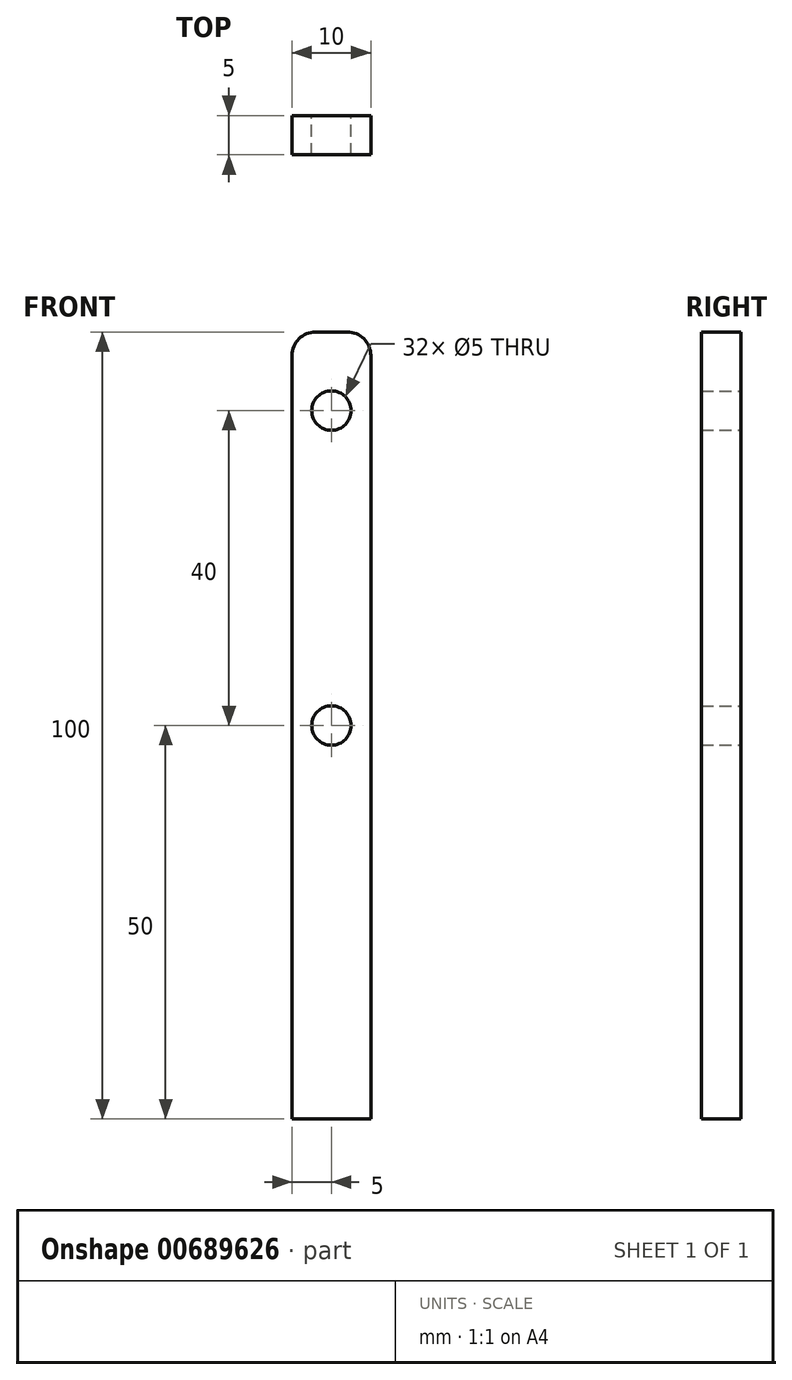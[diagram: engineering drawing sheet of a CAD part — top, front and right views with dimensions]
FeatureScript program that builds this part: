
annotation { "Feature Type Name" : "Feature", "Feature Type Description" : "" }
export const myFeature = defineFeature(function(context is Context, id is Id, definition is map)
    precondition{}
    {
        {
            var Q0;
            Q0=qCreatedBy(makeId("Front.planeOp"),FACE);
            var sketch = newSketch(context, id + "F0", { "sketchPlane" : qUnion([Q0])});
            skLineSegment(sketch, "E0", {"start": v(0, 0) * mm, "end": v(-10, 0) * mm});
            skLineSegment(sketch, "E1", {"start": v(-10, 0) * mm, "end": v(-10, 97) * mm});
            skLineSegment(sketch, "E2", {"start": v(-7, 100) * mm, "end": v(-3, 100) * mm});
            skLineSegment(sketch, "E3", {"start": v(0, 97) * mm, "end": v(0, 0) * mm});
            skCircle(sketch, "E4", {"center": v(-5, 50) * mm, "radius": 2.5 * mm});
            skCircle(sketch, "E5", {"center": v(-5, 90) * mm, "radius": 2.5 * mm});
            skPoint(sketch, "E6.visualSharp", {"position": v(0, 100) * mm});
            skArc(sketch, "E6.filletArc", {"start": v(0, 97) * mm, "mid": v(-0.88, 99.12) * mm, "end": v(-3, 100) * mm});
            skPoint(sketch, "E7.visualSharp", {"position": v(-10, 100) * mm});
            skArc(sketch, "E7.filletArc", {"start": v(-7, 100) * mm, "mid": v(-9.12, 99.12) * mm, "end": v(-10, 97) * mm});
            skSolve(sketch);
        }
        {
            var Q0;
            Q0 = qSketchRegion(id + "F0", true);
            extrude(context, id + "F1", {"entities" : qUnion([Q0]), "depth" : 5 * mm, "offsetDistance" : 25 * mm});
        }
    });
